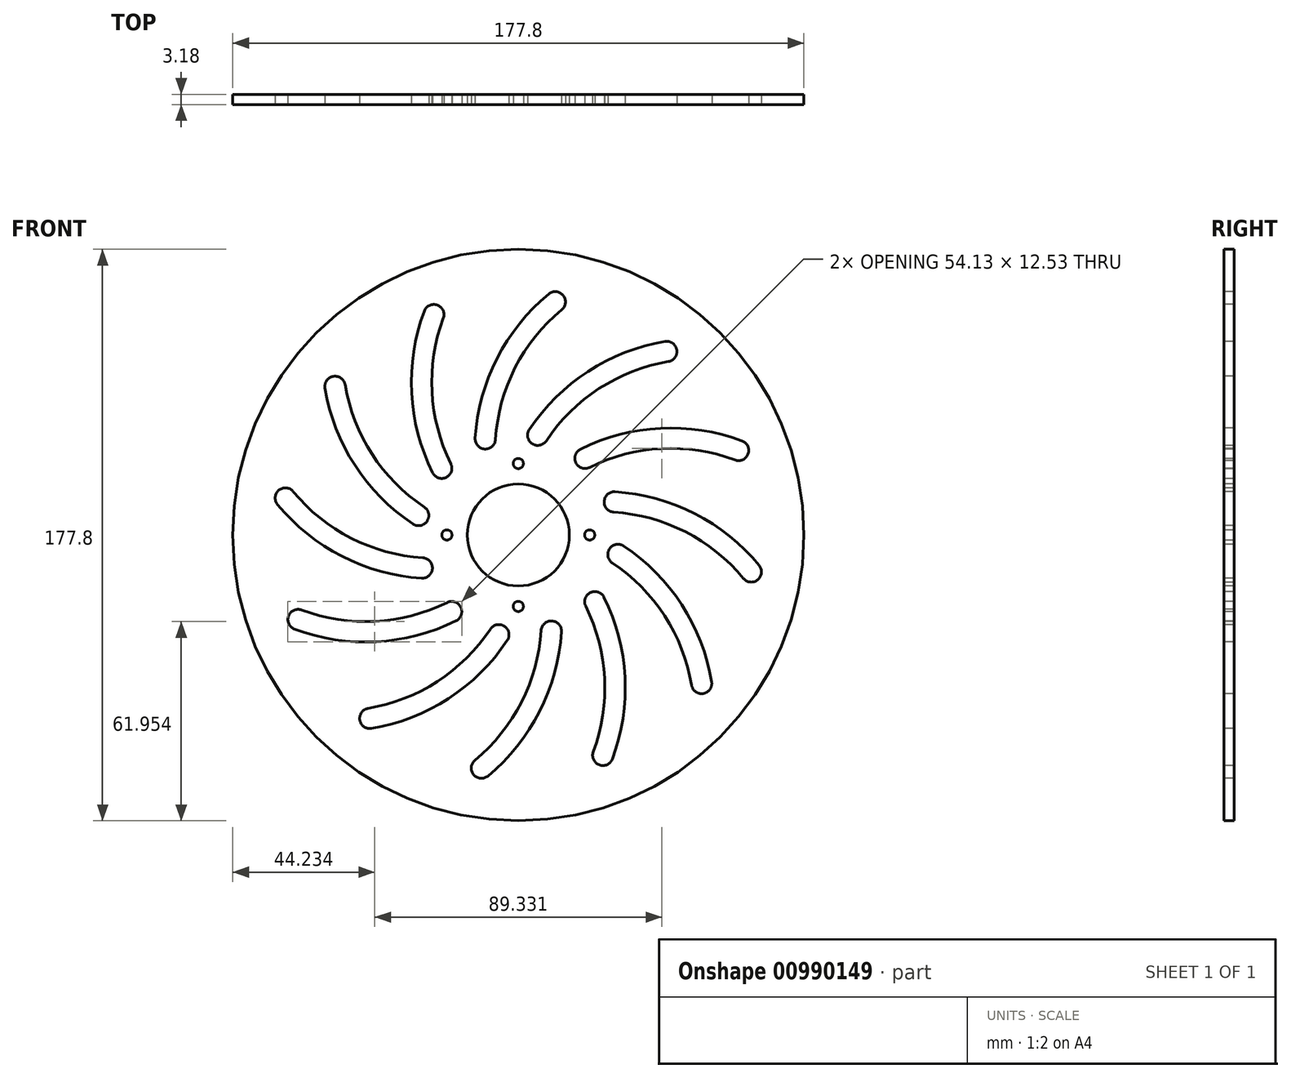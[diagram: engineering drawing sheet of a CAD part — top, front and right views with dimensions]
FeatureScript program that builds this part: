
annotation { "Feature Type Name" : "Feature", "Feature Type Description" : "" }
export const myFeature = defineFeature(function(context is Context, id is Id, definition is map)
    precondition{}
    {
        {
            var Q0;
            Q0=qCreatedBy(makeId("Front.planeOp"),FACE);
            var sketch = newSketch(context, id + "F0", { "sketchPlane" : qUnion([Q0])});
            skCircle(sketch, "E0", {"center": v(0, 0) * mm, "radius": 15.88 * mm});
            skCircle(sketch, "E1", {"center": v(0, 0) * mm, "radius": 88.9 * mm});
            skArc(sketch, "E2", {"start": v(68.56, 26.31) * mm, "mid": v(44.4, 30.04) * mm, "end": v(20.77, 23.85) * mm, "construction": true});
            skArc(sketch, "E3.0.startCap", {"start": v(69.67, 29.29) * mm, "mid": v(71.53, 25.2) * mm, "end": v(67.45, 23.34) * mm});
            skArc(sketch, "E3.0.endCap", {"start": v(22.18, 21) * mm, "mid": v(17.93, 22.44) * mm, "end": v(19.36, 26.7) * mm});
            skArc(sketch, "E3.0.left", {"start": v(67.45, 23.34) * mm, "mid": v(44.57, 26.86) * mm, "end": v(22.18, 21) * mm});
            skArc(sketch, "E3.0.right", {"start": v(69.67, 29.29) * mm, "mid": v(44.24, 33.2) * mm, "end": v(19.36, 26.7) * mm});
            skArc(sketch, "E4.1.0", {"start": v(45.69, 60.2) * mm, "mid": v(49.35, 57.6) * mm, "end": v(46.74, 53.94) * mm});
            skArc(sketch, "E4.1.1", {"start": v(45.69, 60.2) * mm, "mid": v(21.71, 50.88) * mm, "end": v(3.42, 32.8) * mm});
            skArc(sketch, "E4.1.2", {"start": v(46.74, 53.94) * mm, "mid": v(25.17, 45.55) * mm, "end": v(8.7, 29.28) * mm});
            skArc(sketch, "E4.1.3", {"start": v(8.7, 29.28) * mm, "mid": v(4.3, 28.4) * mm, "end": v(3.42, 32.8) * mm});
            skArc(sketch, "E4.2.0", {"start": v(9.47, 74.98) * mm, "mid": v(13.94, 74.55) * mm, "end": v(13.51, 70.08) * mm});
            skArc(sketch, "E4.2.1", {"start": v(9.47, 74.98) * mm, "mid": v(-6.64, 54.92) * mm, "end": v(-13.44, 30.11) * mm});
            skArc(sketch, "E4.2.2", {"start": v(13.51, 70.08) * mm, "mid": v(-0.98, 52.03) * mm, "end": v(-7.1, 29.71) * mm});
            skArc(sketch, "E4.2.3", {"start": v(-7.1, 29.71) * mm, "mid": v(-10.47, 26.74) * mm, "end": v(-13.44, 30.11) * mm});
            skArc(sketch, "E4.3.0", {"start": v(-29.29, 69.67) * mm, "mid": v(-25.2, 71.53) * mm, "end": v(-23.34, 67.45) * mm});
            skArc(sketch, "E4.3.1", {"start": v(-29.29, 69.67) * mm, "mid": v(-33.2, 44.24) * mm, "end": v(-26.7, 19.36) * mm});
            skArc(sketch, "E4.3.2", {"start": v(-23.34, 67.45) * mm, "mid": v(-26.86, 44.57) * mm, "end": v(-21, 22.18) * mm});
            skArc(sketch, "E4.3.3", {"start": v(-21, 22.18) * mm, "mid": v(-22.44, 17.93) * mm, "end": v(-26.7, 19.36) * mm});
            skArc(sketch, "E4.4.0", {"start": v(-60.2, 45.69) * mm, "mid": v(-57.6, 49.35) * mm, "end": v(-53.94, 46.74) * mm});
            skArc(sketch, "E4.4.1", {"start": v(-60.2, 45.69) * mm, "mid": v(-50.88, 21.71) * mm, "end": v(-32.8, 3.42) * mm});
            skArc(sketch, "E4.4.2", {"start": v(-53.94, 46.74) * mm, "mid": v(-45.55, 25.17) * mm, "end": v(-29.28, 8.7) * mm});
            skArc(sketch, "E4.4.3", {"start": v(-29.28, 8.7) * mm, "mid": v(-28.4, 4.3) * mm, "end": v(-32.8, 3.42) * mm});
            skArc(sketch, "E4.5.0", {"start": v(-74.98, 9.47) * mm, "mid": v(-74.55, 13.94) * mm, "end": v(-70.08, 13.51) * mm});
            skArc(sketch, "E4.5.1", {"start": v(-74.98, 9.47) * mm, "mid": v(-54.92, -6.64) * mm, "end": v(-30.11, -13.44) * mm});
            skArc(sketch, "E4.5.2", {"start": v(-70.08, 13.51) * mm, "mid": v(-52.03, -0.98) * mm, "end": v(-29.71, -7.1) * mm});
            skArc(sketch, "E4.5.3", {"start": v(-29.71, -7.1) * mm, "mid": v(-26.74, -10.47) * mm, "end": v(-30.11, -13.44) * mm});
            skArc(sketch, "E4.6.0", {"start": v(-69.67, -29.29) * mm, "mid": v(-71.53, -25.2) * mm, "end": v(-67.45, -23.34) * mm});
            skArc(sketch, "E4.6.1", {"start": v(-69.67, -29.29) * mm, "mid": v(-44.24, -33.2) * mm, "end": v(-19.36, -26.7) * mm});
            skArc(sketch, "E4.6.2", {"start": v(-67.45, -23.34) * mm, "mid": v(-44.57, -26.86) * mm, "end": v(-22.18, -21) * mm});
            skArc(sketch, "E4.6.3", {"start": v(-22.18, -21) * mm, "mid": v(-17.93, -22.44) * mm, "end": v(-19.36, -26.7) * mm});
            skArc(sketch, "E4.7.0", {"start": v(-45.69, -60.2) * mm, "mid": v(-49.35, -57.6) * mm, "end": v(-46.74, -53.94) * mm});
            skArc(sketch, "E4.7.1", {"start": v(-45.69, -60.2) * mm, "mid": v(-21.71, -50.88) * mm, "end": v(-3.42, -32.8) * mm});
            skArc(sketch, "E4.7.2", {"start": v(-46.74, -53.94) * mm, "mid": v(-25.17, -45.55) * mm, "end": v(-8.7, -29.28) * mm});
            skArc(sketch, "E4.7.3", {"start": v(-8.7, -29.28) * mm, "mid": v(-4.3, -28.4) * mm, "end": v(-3.42, -32.8) * mm});
            skArc(sketch, "E4.8.0", {"start": v(-9.47, -74.98) * mm, "mid": v(-13.94, -74.55) * mm, "end": v(-13.51, -70.08) * mm});
            skArc(sketch, "E4.8.1", {"start": v(-9.47, -74.98) * mm, "mid": v(6.64, -54.92) * mm, "end": v(13.44, -30.11) * mm});
            skArc(sketch, "E4.8.2", {"start": v(-13.51, -70.08) * mm, "mid": v(0.98, -52.03) * mm, "end": v(7.1, -29.71) * mm});
            skArc(sketch, "E4.8.3", {"start": v(7.1, -29.71) * mm, "mid": v(10.47, -26.74) * mm, "end": v(13.44, -30.11) * mm});
            skArc(sketch, "E4.9.0", {"start": v(29.29, -69.67) * mm, "mid": v(25.2, -71.53) * mm, "end": v(23.34, -67.45) * mm});
            skArc(sketch, "E4.9.1", {"start": v(29.29, -69.67) * mm, "mid": v(33.2, -44.24) * mm, "end": v(26.7, -19.36) * mm});
            skArc(sketch, "E4.9.2", {"start": v(23.34, -67.45) * mm, "mid": v(26.86, -44.57) * mm, "end": v(21, -22.18) * mm});
            skArc(sketch, "E4.9.3", {"start": v(21, -22.18) * mm, "mid": v(22.44, -17.93) * mm, "end": v(26.7, -19.36) * mm});
            skArc(sketch, "E4.10.0", {"start": v(60.2, -45.69) * mm, "mid": v(57.6, -49.35) * mm, "end": v(53.94, -46.74) * mm});
            skArc(sketch, "E4.10.1", {"start": v(60.2, -45.69) * mm, "mid": v(50.88, -21.71) * mm, "end": v(32.8, -3.42) * mm});
            skArc(sketch, "E4.10.2", {"start": v(53.94, -46.74) * mm, "mid": v(45.55, -25.17) * mm, "end": v(29.28, -8.7) * mm});
            skArc(sketch, "E4.10.3", {"start": v(29.28, -8.7) * mm, "mid": v(28.4, -4.3) * mm, "end": v(32.8, -3.42) * mm});
            skArc(sketch, "E4.11.0", {"start": v(74.98, -9.47) * mm, "mid": v(74.55, -13.94) * mm, "end": v(70.08, -13.51) * mm});
            skArc(sketch, "E4.11.1", {"start": v(74.98, -9.47) * mm, "mid": v(54.92, 6.64) * mm, "end": v(30.11, 13.44) * mm});
            skArc(sketch, "E4.11.2", {"start": v(70.08, -13.51) * mm, "mid": v(52.03, 0.98) * mm, "end": v(29.71, 7.1) * mm});
            skArc(sketch, "E4.11.3", {"start": v(29.71, 7.1) * mm, "mid": v(26.74, 10.47) * mm, "end": v(30.11, 13.44) * mm});
            skCircle(sketch, "E5", {"center": v(0, 22.23) * mm, "radius": 1.59 * mm});
            skCircle(sketch, "E6", {"center": v(0, 0) * mm, "radius": 22.23 * mm, "construction": true});
            skLineSegment(sketch, "E7", {"start": v(0, 0) * mm, "end": v(0, 22.23) * mm, "construction": true});
            skCircle(sketch, "E8.1.0", {"center": v(-22.23, 0) * mm, "radius": 1.59 * mm});
            skCircle(sketch, "E8.2.0", {"center": v(0, -22.23) * mm, "radius": 1.59 * mm});
            skCircle(sketch, "E8.3.0", {"center": v(22.23, 0) * mm, "radius": 1.59 * mm});
            skSolve(sketch);
        }
        {
            var Q0;
            Q0=makeQuery(id+"F0.imprint","IMPRINT",FACE,{"disambiguationData":[TD([[makeQuery(id+"F0.imprint","IMPRINT",EDGE,{"derivedFrom":sQuery(id+"F0.wireOp",EDGE,"E0")}),-1.0]])]});
            extrude(context, id + "F1", {"entities" : qUnion([Q0]), "oppositeDirection" : true, "depth" : 3.17 * mm, "offsetDistance" : 25.4 * mm});
        }
    });
